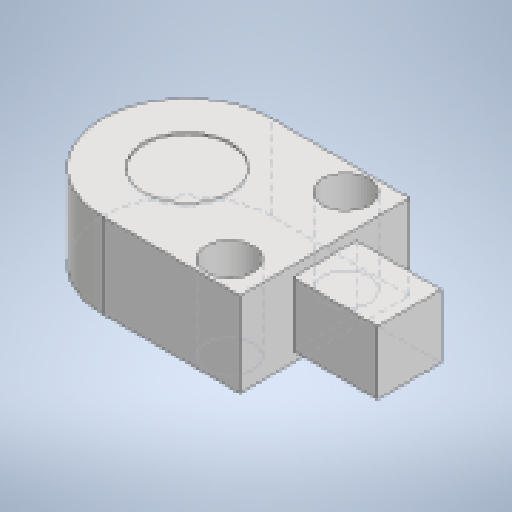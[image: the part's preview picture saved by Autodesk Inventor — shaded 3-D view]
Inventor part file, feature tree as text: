
AUTODESK INVENTOR PART (.ipt)
format: ipt  version: 2023 (Build 270158000, 158)  size: 167,424 bytes
history: native  units: mm
features: extrude x4, sketch x4
ambient origin geometry x8: Origin, YZ Plane, XZ Plane, XY Plane, X Axis, Y Axis, Z Axis, Center Point
bodies: Solid1 (feature_tree)
feature tree (8):
  extrude  "Extrusion1"  Depth=8.0mm
  extrude  "Extrusion2"  Depth=5.5mm
  extrude  "Extrusion3"  Depth=1.75mm
  extrude  "Extrusion4"  Depth=10.0mm
  sketch  "Sketch1"  dims[d0=8.0mm d1=6.5mm]
  sketch  "Sketch2"  dims[d2=5.5mm d3=2.75mm]
  sketch  "Sketch3"  dims[d4=1.75mm d5=1.75mm]
  sketch  "Sketch4"  dims[d6=2.2mm d7=2.2mm d8=4.0mm d9=0.0mm d10=3.0mm d11=3.0mm d12=0.5mm d13=5.5mm d14=4.0mm d15=0.0mm d16=4.1mm d17=0.1mm d18=0.0mm d19=2.2mm d20=10.0mm d21=0.0mm]
